# Revit family: BIM_CHV_DUAL PLATE CHECK VALVE_DN40-400_PN10-16-25_ANSI125-150_MODEL-C
name_source: partatom
category: Generic Models
revit_build: Autodesk Revit 2017 (Build: 20160225_1515(x64)
units: mm (PartAtom-declared; Revit-internal decimal feet)

## family parameters
Always vertical = Yes
Can host rebar = No
Cut with Voids When Loaded = No
Part Type = Normal
Room Calculation Point = No
Round Connector Dimension = Use Diameter
Shared = No
Work Plane-Based = No

## types (47) — shared parameters

## per-type parameters (varying)
| type | DN40_PN10/16/25 | DN50_PN10/16/25 | DN65_PN10/16/25 | DN80_PN10/16/25 | NOMINAL_DIA |
| DN40_PN10 | Yes | No | No | No | 40 mm  [stored 0.131234 ft] |
| DN40_PN16 | Yes | No | No | No | 40 mm  [stored 0.131234 ft] |
| DN40_PN25 | Yes | No | No | No | 40 mm  [stored 0.131234 ft] |
| DN50_ANSI125/150 | No | No | No | No | 50 mm  [stored 0.164042 ft] |
| DN50_PN10 | No | Yes | No | No | 50 mm  [stored 0.164042 ft] |
| DN50_PN16 | No | Yes | No | No | 50 mm  [stored 0.164042 ft] |
| DN50_PN25 | No | Yes | No | No | 50 mm  [stored 0.164042 ft] |
| DN65_ANSI125/150 | No | No | No | No | 65 mm  [stored 0.213255 ft] |
| DN65_PN10 | No | No | Yes | No | 65 mm  [stored 0.213255 ft] |
| DN65_PN16 | No | No | Yes | No | 65 mm  [stored 0.213255 ft] |
| DN65_PN25 | No | No | Yes | No | 65 mm  [stored 0.213255 ft] |
| DN80_ANSI125/150 | No | No | No | No | 80 mm  [stored 0.262467 ft] |
| DN80_PN10 | No | No | No | Yes | 80 mm  [stored 0.262467 ft] |
| DN100_PN10 | No | No | No | No | 100 mm  [stored 0.328084 ft] |
| DN100_PN16 | No | No | No | No | 100 mm  [stored 0.328084 ft] |
| DN100_PN25 | No | No | No | No | 100 mm  [stored 0.328084 ft] |
| DN100_ANSI125/150 | No | No | No | No | 100 mm  [stored 0.328084 ft] |
| DN125_PN10 | No | No | No | No | 125 mm  [stored 0.410105 ft] |
| DN125_PN16 | No | No | No | No | 125 mm  [stored 0.410105 ft] |
| DN125_PN25 | No | No | No | No | 125 mm  [stored 0.410105 ft] |
| DN125_ANSI125/150 | No | No | No | No | 125 mm  [stored 0.410105 ft] |
| DN150_PN10 | No | No | No | No | 150 mm  [stored 0.492126 ft] |
| DN150_PN16 | No | No | No | No | 150 mm  [stored 0.492126 ft] |
| DN150_PN25 | No | No | No | No | 150 mm  [stored 0.492126 ft] |
| DN150_ANSI125/150 | No | No | No | No | 150 mm  [stored 0.492126 ft] |
| DN200_PN10 | No | No | No | No | 200 mm  [stored 0.656168 ft] |
| DN200_PN16 | No | No | No | No | 200 mm  [stored 0.656168 ft] |
| DN200_ANSI125/150 | No | No | No | No | 200 mm  [stored 0.656168 ft] |
| DN200_PN25 | No | No | No | No | 200 mm  [stored 0.656168 ft] |
| DN250_PN10 | No | No | No | No | 250 mm  [stored 0.82021 ft] |
| DN250_PN16 | No | No | No | No | 250 mm  [stored 0.82021 ft] |
| DN250_PN25 | No | No | No | No | 250 mm  [stored 0.82021 ft] |
| DN250_ANSI125/150 | No | No | No | No | 250 mm  [stored 0.82021 ft] |
| DN300_ANSI125/150 | No | No | No | No | 300 mm |
| DN300_PN10 | No | No | No | No | 300 mm |
| DN300_PN16 | No | No | No | No | 300 mm |
| DN300_PN25 | No | No | No | No | 300 mm |
| DN350_ANSI125/150 | No | No | No | No | 350 mm  [stored 1.14829 ft] |
| DN350_PN10 | No | No | No | No | 350 mm  [stored 1.14829 ft] |
| DN350_PN16 | No | No | No | No | 350 mm  [stored 1.14829 ft] |
| DN350_PN25 | No | No | No | No | 350 mm  [stored 1.14829 ft] |
| DN400_PN10 | No | No | No | No | 400 mm  [stored 1.31234 ft] |
| DN400_PN16 | No | No | No | No | 400 mm  [stored 1.31234 ft] |
| DN400_PN25 | No | No | No | No | 400 mm  [stored 1.31234 ft] |
| DN400_ANSI125/150 | No | No | No | No | 400 mm  [stored 1.31234 ft] |
| DN80_PN16 | No | No | No | Yes | 80 mm  [stored 0.262467 ft] |
| DN80_PN25 | No | No | No | Yes | 80 mm  [stored 0.262467 ft] |

type visibility flags (boolean, named after types; folded from table):
- DN40_PN10: Yes: (none)
- DN40_PN16: Yes: (none)
- DN40_PN25: Yes: (none)
- DN50_ANSI125/150: Yes: DN50_ANSI125/150
- DN50_PN10: Yes: (none)
- DN50_PN16: Yes: (none)
- DN50_PN25: Yes: (none)
- DN65_ANSI125/150: Yes: DN65_ANSI125/150
- DN65_PN10: Yes: (none)
- DN65_PN16: Yes: (none)
- DN65_PN25: Yes: (none)
- DN80_ANSI125/150: Yes: DN80_ANSI125/150
- DN80_PN10: Yes: (none)
- DN100_PN10: Yes: DN100_PN10/16
- DN100_PN16: Yes: DN100_PN10/16
- DN100_PN25: Yes: DN100_PN25_ANSI125/150
- DN100_ANSI125/150: Yes: DN100_PN25_ANSI125/150
- DN125_PN10: Yes: DN125_PN10/16/25_ANSI125/150
- DN125_PN16: Yes: DN125_PN10/16/25_ANSI125/150
- DN125_PN25: Yes: DN125_PN10/16/25_ANSI125/150
- DN125_ANSI125/150: Yes: DN125_PN10/16/25_ANSI125/150
- DN150_PN10: Yes: DN150_PN10/16/25_ANSI125/150
- DN150_PN16: Yes: DN150_PN10/16/25_ANSI125/150
- DN150_PN25: Yes: DN150_PN10/16/25_ANSI125/150
- DN150_ANSI125/150: Yes: DN150_PN10/16/25_ANSI125/150
- DN200_PN10: Yes: DN200_PN10/16_ANSI125/150
- DN200_PN16: Yes: DN200_PN10/16_ANSI125/150
- DN200_ANSI125/150: Yes: DN200_PN10/16_ANSI125/150
- DN200_PN25: Yes: DN200_PN25
- DN250_PN10: Yes: DN250_PN10/16
- DN250_PN16: Yes: DN250_PN10/16
- DN250_PN25: Yes: DN250_PN25_ANSI125/150
- DN250_ANSI125/150: Yes: DN250_PN25_ANSI125/150
- DN300_ANSI125/150: Yes: DN300_ANSI125/150
- DN300_PN10: Yes: DN300_PN10/16
- DN300_PN16: Yes: DN300_PN10/16
- DN300_PN25: Yes: DN300_PN25
- DN350_ANSI125/150: Yes: DN350_ANSI125/150
- DN350_PN10: Yes: DN350_PN10/16
- DN350_PN16: Yes: DN350_PN10/16
- DN350_PN25: Yes: DN350_PN25
- DN400_PN10: Yes: DN400_PN10/16
- DN400_PN16: Yes: DN400_PN10/16
- DN400_PN25: Yes: DN400_PN25_ANSI125/150
- DN400_ANSI125/150: Yes: DN400_PN25_ANSI125/150
- DN80_PN16: Yes: (none)
- DN80_PN25: Yes: (none)

note: [stored X ft] marks values corroborated as IEEE doubles in the binary element streams (Revit-internal decimal feet)

## geometry (parser evidence)
native form markers: Sweep x59
no freeform markers — native parametric forms only
